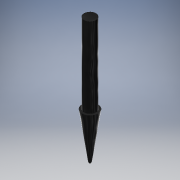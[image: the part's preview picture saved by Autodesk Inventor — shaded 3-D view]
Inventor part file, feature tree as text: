
AUTODESK INVENTOR PART (.ipt)
format: ipt  version: 2017 (Build 210142000, 142)  size: 104,448 bytes
history: native  units: mm
features: revolve x1, sketch x1
ambient origin geometry x8: Origin, YZ Plane, XZ Plane, XY Plane, X Axis, Y Axis, Z Axis, Center Point
bodies: Solid1 (feature_tree)
feature tree (2):
  revolve  "Revolution1"  [1 undecoded]
  sketch  "Sketch1"  dims[d7=0.25mm d9=0.001mm d11=90.0deg]
note: 1 required parameter value undecoded (feature->parameter linkage not recoverable at this tier; creation-order binding heuristic only, values carry confidence <= 0.55)
